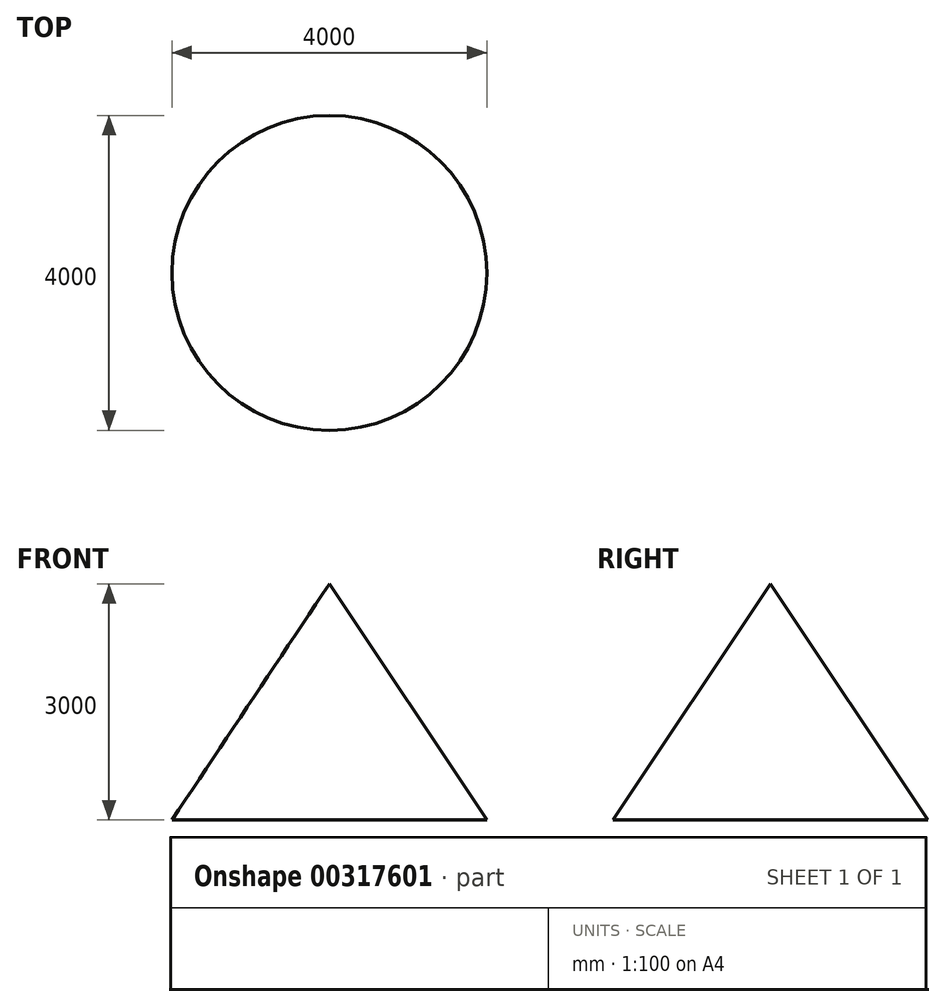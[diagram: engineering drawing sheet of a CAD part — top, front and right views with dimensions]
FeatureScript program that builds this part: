
annotation { "Feature Type Name" : "Feature", "Feature Type Description" : "" }
export const myFeature = defineFeature(function(context is Context, id is Id, definition is map)
    precondition{}
    {
        {
            var Q0;
            Q0=qCreatedBy(makeId("Front.planeOp"),FACE);
            var sketch = newSketch(context, id + "F0", { "sketchPlane" : qUnion([Q0])});
            skLineSegment(sketch, "E0", {"start": v(0, 0) * mm, "end": v(0, -3000) * mm});
            skLineSegment(sketch, "E1", {"start": v(0, -3000) * mm, "end": v(2000, -3000) * mm});
            skLineSegment(sketch, "E2", {"start": v(0, 0) * mm, "end": v(2000, -3000) * mm});
            skSolve(sketch);
        }
        {
            var Q0;
            Q0 = qSketchRegion(id + "F0", true);
            var Q1;
            Q1=sQuery(id+"F0.wireOp",EDGE,"E0");
            revolve(context, id + "F1", {"entities" : qUnion([Q0]), "axis" : qUnion([Q1]), "revolveType" : RevolveType.FULL});
        }
    });
